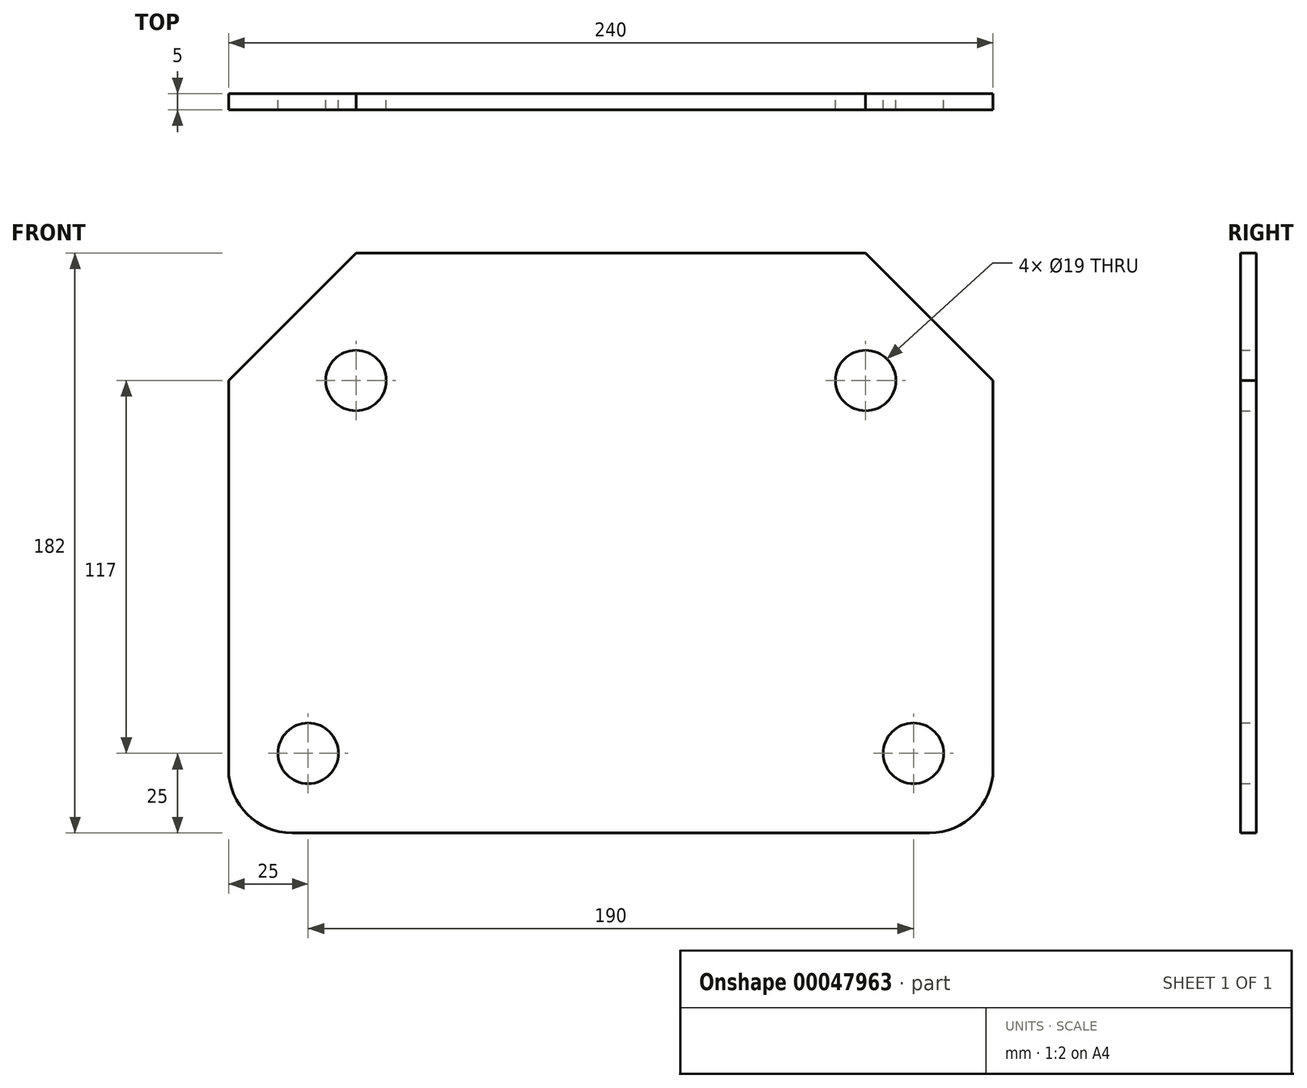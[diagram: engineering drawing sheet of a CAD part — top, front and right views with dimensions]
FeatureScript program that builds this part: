
annotation { "Feature Type Name" : "Feature", "Feature Type Description" : "" }
export const myFeature = defineFeature(function(context is Context, id is Id, definition is map)
    precondition{}
    {
        {
            var Q0;
            Q0=qCreatedBy(makeId("Front.planeOp"),FACE);
            var sketch = newSketch(context, id + "F0", { "sketchPlane" : qUnion([Q0])});
            skLineSegment(sketch, "E0.rect.bottom", {"start": v(80, 91) * mm, "end": v(-80, 91) * mm});
            skLineSegment(sketch, "E0.rect.top", {"start": v(120, -91) * mm, "end": v(-120, -91) * mm});
            skLineSegment(sketch, "E0.rect.left", {"start": v(120, 51) * mm, "end": v(120, -91) * mm});
            skLineSegment(sketch, "E0.rect.right", {"start": v(-120, 51) * mm, "end": v(-120, -91) * mm});
            skPoint(sketch, "E0.rect.middle", {"position": v(0, 0) * mm});
            skLineSegment(sketch, "E1", {"start": v(-120, 51) * mm, "end": v(-80, 91) * mm});
            skLineSegment(sketch, "E2", {"start": v(120, 51) * mm, "end": v(80, 91) * mm});
            skPoint(sketch, "E3.orphan", {"position": v(-120, 91) * mm});
            skPoint(sketch, "E4.orphan", {"position": v(120, 91) * mm});
            skLineSegment(sketch, "E5", {"start": v(-80, 91) * mm, "end": v(-80, 26.97) * mm, "construction": true});
            skLineSegment(sketch, "E6", {"start": v(-120, 51) * mm, "end": v(120, 51) * mm, "construction": true});
            skLineSegment(sketch, "E7", {"start": v(80, 91) * mm, "end": v(80, 51) * mm, "construction": true});
            skCircle(sketch, "E8", {"center": v(-80, 51) * mm, "radius": 9.5 * mm});
            skPoint(sketch, "E8.centerSnap0", {"position": v(-80, 58.99) * mm});
            skCircle(sketch, "E9", {"center": v(80, 51) * mm, "radius": 9.5 * mm});
            skLineSegment(sketch, "E10", {"start": v(-120, -91) * mm, "end": v(-120, -66) * mm, "construction": true});
            skLineSegment(sketch, "E11", {"start": v(-120, -66) * mm, "end": v(120, -66) * mm, "construction": true});
            skLineSegment(sketch, "E12", {"start": v(120, -66) * mm, "end": v(120, -91) * mm, "construction": true});
            skLineSegment(sketch, "E13", {"start": v(-120, -66) * mm, "end": v(-95, -66) * mm});
            skLineSegment(sketch, "E14", {"start": v(120, -66) * mm, "end": v(95, -66) * mm});
            skCircle(sketch, "E15", {"center": v(95, -66) * mm, "radius": 9.5 * mm});
            skCircle(sketch, "E16", {"center": v(-95, -66) * mm, "radius": 9.5 * mm});
            skSolve(sketch);
        }
        {
            var Q0;
            Q0 = qSketchRegion(id + "F0", true);
            extrude(context, id + "F1", {"entities" : qUnion([Q0]), "depth" : 5 * mm});
        }
        {
            var Q0;
            Q0=makeQuery(id+"F1.opExtrude","SWEPT_EDGE",EDGE,{"disambiguationData":[OSD([sQuery(id+"F0.wireOp",EDGE,"E0.rect.top"),sQuery(id+"F0.wireOp",EDGE,"E0.rect.right")])]});
            var Q1;
            Q1=makeQuery(id+"F1.opExtrude","SWEPT_EDGE",EDGE,{"disambiguationData":[OSD([sQuery(id+"F0.wireOp",EDGE,"E0.rect.top"),sQuery(id+"F0.wireOp",EDGE,"E0.rect.left")])]});
            fillet(context, id + "F2", {"entities" : qUnion([Q0, Q1]), "radius" : 20 * mm, "tangentPropagation" : true, "allowEdgeOverflow" : false});
        }
    });
